# Revit family: 41-Percha Palermo
name_source: partatom
category: Aparatos sanitarios
revit_build: Autodesk Revit 2018 (Build: 20170223_1515(x64)
units: mm (PartAtom-declared; Revit-internal decimal feet)

## family parameters
Anfitrión = Cara
Compartido = No
Corte con vacíos al cargar = No
Cota de conector redondo = Diámetro de uso
Número OmniClass = 23.45.00.00
Punto de cálculo de habitación = No
Tipo de pieza = Normal
Título OmniClass = Sanitary, Laundry, and Cleaning Equipment

## types (1)
- 41-Percha Palermo
    Acabado = Brillante
    Color = Cromo
    Descripción IFC = Percha Palermo
    Duración Garantía Unidad = Año
    Elevación por defecto = 0 mm  [stored 0 ft]
    Fabricante = www.corona.com.co
    Material Acabado = Cromo-Corona
    Material de Fabricación = Latón
    Nombre = Percha
    Nombre del Fabricante = Corona
    Tráfico = Residencial

note: [stored X ft] marks values corroborated as IEEE doubles in the binary element streams (Revit-internal decimal feet)

## geometry (parser evidence)
native form markers: Sweep x2
no freeform markers — native parametric forms only
